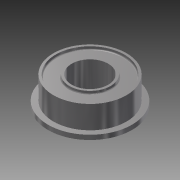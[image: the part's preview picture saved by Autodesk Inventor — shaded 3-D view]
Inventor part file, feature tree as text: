
AUTODESK INVENTOR PART (.ipt)
format: ipt  version: 2013 (Build 170138000, 138)  size: 157,184 bytes
history: native  units: mm
features: sketch x5, extrude x4, other x1, hole x1, fillet x1
ambient origin geometry x1: Origin
feature tree (12):
  other  "ソリッド1"
  extrude  "押し出し1"  Depth=9.2mm
  extrude  "押し出し2"  Depth=0.5mm TaperAngle=0.0deg
  hole  "穴1"  [1 undecoded]
  extrude  "押し出し3"  Depth=2.5mm TaperAngle=0.0deg
  extrude  "押し出し4"  Depth=4.0mm
  fillet  "フィレット1"  Radius=4.5mm
  sketch  "スケッチ1"
  sketch  "スケッチ2"
  sketch  "スケッチ3"
  sketch  "スケッチ4"
  sketch  "スケッチ5"
note: 1 required parameter value undecoded (feature->parameter linkage not recoverable at this tier; creation-order binding heuristic only, values carry confidence <= 0.55)
